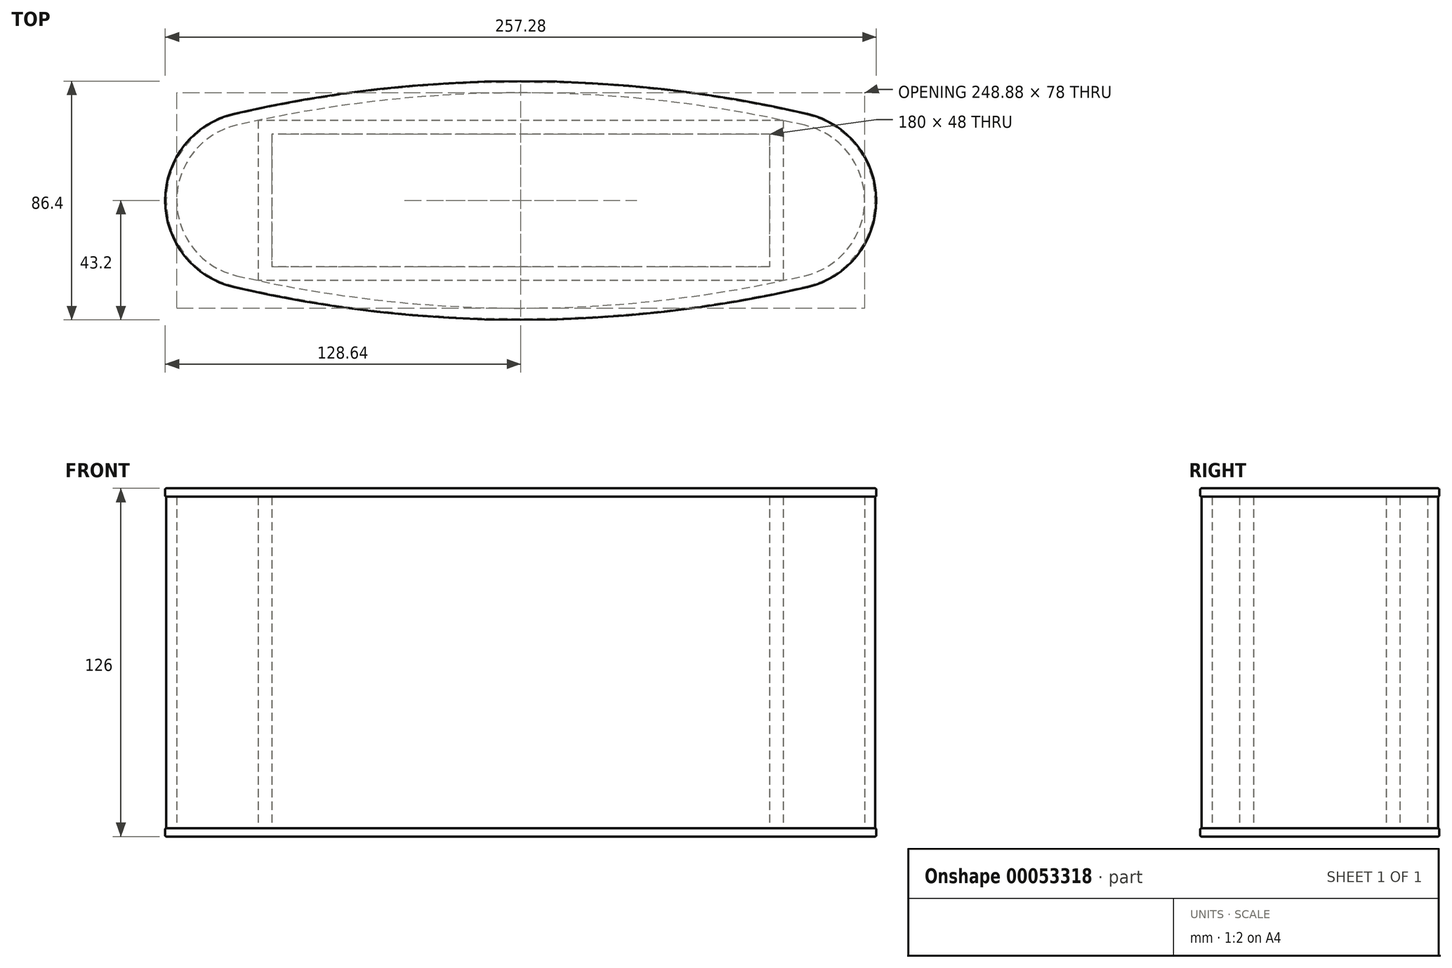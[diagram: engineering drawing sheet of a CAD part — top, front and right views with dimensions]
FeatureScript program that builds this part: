
annotation { "Feature Type Name" : "Feature", "Feature Type Description" : "" }
export const myFeature = defineFeature(function(context is Context, id is Id, definition is map)
    precondition{}
    {
        {
            var Q0;
            Q0=qCreatedBy(makeId("Top.planeOp"),FACE);
            var sketch = newSketch(context, id + "F0", { "sketchPlane" : qUnion([Q0])});
            skLineSegment(sketch, "E0.rect.bottom", {"start": v(90, 24) * mm, "end": v(-90, 24) * mm});
            skLineSegment(sketch, "E0.rect.top", {"start": v(90, -24) * mm, "end": v(-90, -24) * mm});
            skLineSegment(sketch, "E0.rect.left", {"start": v(90, 24) * mm, "end": v(90, -24) * mm});
            skLineSegment(sketch, "E0.rect.right", {"start": v(-90, 24) * mm, "end": v(-90, -24) * mm});
            skPoint(sketch, "E0.rect.middle", {"position": v(0, 0) * mm});
            skLineSegment(sketch, "E1.rect.bottom", {"start": v(95, 29) * mm, "end": v(-95, 29) * mm});
            skLineSegment(sketch, "E1.rect.top", {"start": v(95, -29) * mm, "end": v(-95, -29) * mm});
            skLineSegment(sketch, "E1.rect.left", {"start": v(95, 29) * mm, "end": v(95, -29) * mm});
            skLineSegment(sketch, "E1.rect.right", {"start": v(-95, 29) * mm, "end": v(-95, -29) * mm});
            skArc(sketch, "E2", {"start": v(102.74, 27.28) * mm, "mid": v(0, 39) * mm, "end": v(-102.74, 27.28) * mm});
            skArc(sketch, "E3", {"start": v(-102.74, -27.28) * mm, "mid": v(0, -39) * mm, "end": v(102.74, -27.28) * mm});
            skArc(sketch, "E4", {"start": v(-102.74, 27.28) * mm, "mid": v(-124.44, 0) * mm, "end": v(-102.74, -27.28) * mm});
            skArc(sketch, "E5", {"start": v(102.74, -27.28) * mm, "mid": v(124.44, 0) * mm, "end": v(102.74, 27.28) * mm});
            skArc(sketch, "E6.0", {"start": v(103.6, 30.98) * mm, "mid": v(0, 42.8) * mm, "end": v(-103.6, 30.98) * mm});
            skArc(sketch, "E6.1", {"start": v(103.6, -30.98) * mm, "mid": v(128.24, 0) * mm, "end": v(103.6, 30.98) * mm});
            skArc(sketch, "E6.2", {"start": v(-103.6, -30.98) * mm, "mid": v(0, -42.8) * mm, "end": v(103.6, -30.98) * mm});
            skArc(sketch, "E6.3", {"start": v(-103.6, 30.98) * mm, "mid": v(-128.24, 0) * mm, "end": v(-103.6, -30.98) * mm});
            skArc(sketch, "E7.0", {"start": v(103.7, 31.37) * mm, "mid": v(0, 43.2) * mm, "end": v(-103.7, 31.37) * mm});
            skArc(sketch, "E7.1", {"start": v(103.7, -31.37) * mm, "mid": v(128.64, 0) * mm, "end": v(103.7, 31.37) * mm});
            skArc(sketch, "E7.2", {"start": v(-103.7, -31.37) * mm, "mid": v(0, -43.2) * mm, "end": v(103.7, -31.37) * mm});
            skArc(sketch, "E7.3", {"start": v(-103.7, 31.37) * mm, "mid": v(-128.64, 0) * mm, "end": v(-103.7, -31.37) * mm});
            skSolve(sketch);
        }
        {
            var Q0;
            {var subQ5=sQuery(id+"F0.wireOp",EDGE,"E4");Q0=makeQuery(id+"F0.imprint","IMPRINT",FACE,{"disambiguationData":[TD([[makeQuery(id+"F0.imprint","IMPRINT",EDGE,{"derivedFrom":subQ5}),-1.0]])]});}
            var Q1;
            Q1=makeQuery(id+"F0.imprint","IMPRINT",FACE,{"disambiguationData":[TD([[makeQuery(id+"F0.imprint","IMPRINT",EDGE,{"derivedFrom":sQuery(id+"F0.wireOp",EDGE,"E0.rect.bottom")}),-1.0]])]});
            extrude(context, id + "F1", {"entities" : qUnion([Q0, Q1]), "depth" : 120 * mm});
        }
        {
            var Q0;
            Q0=qSketchRegion(id+"F0",true);
            var Q1;
            Q1=makeQuery(id+"F1.opExtrude","CAP_FACE",FACE,{"disambiguationData":[OSD([sQuery(id+"F0.wireOp",EDGE,"E2"),sQuery(id+"F0.wireOp",EDGE,"E3"),sQuery(id+"F0.wireOp",EDGE,"E4"),sQuery(id+"F0.wireOp",EDGE,"E5"),sQuery(id+"F0.wireOp",EDGE,"E6.0"),sQuery(id+"F0.wireOp",EDGE,"E6.1"),sQuery(id+"F0.wireOp",EDGE,"E6.2"),sQuery(id+"F0.wireOp",EDGE,"E6.3")])],"isStart":true});
            var Q2;
            {var subQ0=sQuery(id+"F0.wireOp",EDGE,"E1.rect.left");Q2=makeQuery(id+"F0.imprint","IMPRINT",FACE,{"disambiguationData":[TD([[makeQuery(id+"F0.imprint","IMPRINT",EDGE,{"derivedFrom":subQ0}),1.0]])]});}
            var Q3;
            {var subQ0=sQuery(id+"F0.wireOp",EDGE,"E1.rect.bottom");Q3=makeQuery(id+"F0.imprint","IMPRINT",FACE,{"disambiguationData":[TD([[makeQuery(id+"F0.imprint","IMPRINT",EDGE,{"derivedFrom":subQ0}),-1.0]])]});}
            var Q4;
            Q4=makeQuery(id+"F0.imprint","IMPRINT",FACE,{"disambiguationData":[TD([[makeQuery(id+"F0.imprint","IMPRINT",EDGE,{"derivedFrom":sQuery(id+"F0.wireOp",EDGE,"E0.rect.bottom")}),-1.0]])]});
            var Q5;
            Q5=makeQuery(id+"F0.imprint","IMPRINT",FACE,{"disambiguationData":[TD([[makeQuery(id+"F0.imprint","IMPRINT",EDGE,{"derivedFrom":sQuery(id+"F0.wireOp",EDGE,"E0.rect.bottom")}),1.0]])]});
            var Q6;
            {var subQ0=sQuery(id+"F0.wireOp",EDGE,"E1.rect.top");Q6=makeQuery(id+"F0.imprint","IMPRINT",FACE,{"disambiguationData":[TD([[makeQuery(id+"F0.imprint","IMPRINT",EDGE,{"derivedFrom":subQ0}),1.0]])]});}
            var Q7;
            {var subQ0=sQuery(id+"F0.wireOp",EDGE,"E1.rect.right");Q7=makeQuery(id+"F0.imprint","IMPRINT",FACE,{"disambiguationData":[TD([[makeQuery(id+"F0.imprint","IMPRINT",EDGE,{"derivedFrom":subQ0}),-1.0]])]});}
            extrude(context, id + "F2", {"entities" : qUnion([Q0, Q1, Q2, Q3, Q4, Q5, Q6, Q7]), "oppositeDirection" : true, "depth" : 3 * mm});
        }
        {
            var Q0;
            Q0=makeQuery(id+"F2.opExtrude","SWEPT_BODY",BODY,{"disambiguationData":[OSD([sQuery(id+"F0.wireOp",EDGE,"E2"),sQuery(id+"F0.wireOp",EDGE,"E3"),sQuery(id+"F0.wireOp",EDGE,"E4"),sQuery(id+"F0.wireOp",EDGE,"E5"),sQuery(id+"F0.wireOp",EDGE,"E6.0"),sQuery(id+"F0.wireOp",EDGE,"E6.1"),sQuery(id+"F0.wireOp",EDGE,"E6.2"),sQuery(id+"F0.wireOp",EDGE,"E6.3")])]});
            var Q1;
            Q1=makeQuery(id+"F2.opExtrude","SWEPT_BODY",BODY,{"disambiguationData":[OSD([sQuery(id+"F0.wireOp",EDGE,"E6.0"),sQuery(id+"F0.wireOp",EDGE,"E6.1"),sQuery(id+"F0.wireOp",EDGE,"E6.2"),sQuery(id+"F0.wireOp",EDGE,"E6.3"),sQuery(id+"F0.wireOp",EDGE,"E7.0"),sQuery(id+"F0.wireOp",EDGE,"E7.1"),sQuery(id+"F0.wireOp",EDGE,"E7.2"),sQuery(id+"F0.wireOp",EDGE,"E7.3")])]});
            booleanBodies(context, id + "F3", {"operationType" : BooleanOperationType.UNION, "tools" : qUnion([Q0, Q1])});
        }
        {
            var Q0;
            Q0=makeQuery(id+"F2.opExtrude","SWEPT_BODY",BODY,{"disambiguationData":[OSD([sQuery(id+"F0.wireOp",EDGE,"E2"),sQuery(id+"F0.wireOp",EDGE,"E3"),sQuery(id+"F0.wireOp",EDGE,"E4"),sQuery(id+"F0.wireOp",EDGE,"E5")])]});
            var Q1;
            Q1=makeQuery(id+"F2.opExtrude","SWEPT_BODY",BODY,{"disambiguationData":[OSD([sQuery(id+"F0.wireOp",EDGE,"E2"),sQuery(id+"F0.wireOp",EDGE,"E3"),sQuery(id+"F0.wireOp",EDGE,"E4"),sQuery(id+"F0.wireOp",EDGE,"E5"),sQuery(id+"F0.wireOp",EDGE,"E6.0"),sQuery(id+"F0.wireOp",EDGE,"E6.1"),sQuery(id+"F0.wireOp",EDGE,"E6.2"),sQuery(id+"F0.wireOp",EDGE,"E6.3")])]});
            booleanBodies(context, id + "F4", {"operationType" : BooleanOperationType.UNION, "tools" : qUnion([Q0, Q1])});
        }
        {
            var Q0;
            Q0=makeQuery(id+"F1.opExtrude","CAP_FACE",FACE,{"disambiguationData":[OSD([sQuery(id+"F0.wireOp",EDGE,"E2"),sQuery(id+"F0.wireOp",EDGE,"E3"),sQuery(id+"F0.wireOp",EDGE,"E4"),sQuery(id+"F0.wireOp",EDGE,"E5"),sQuery(id+"F0.wireOp",EDGE,"E6.0"),sQuery(id+"F0.wireOp",EDGE,"E6.1"),sQuery(id+"F0.wireOp",EDGE,"E6.2"),sQuery(id+"F0.wireOp",EDGE,"E6.3")])],"isStart":false});
            var sketch = newSketch(context, id + "F5", { "sketchPlane" : qUnion([Q0])});
            skArc(sketch, "E8.0", {"start": v(-103.7, -31.37) * mm, "mid": v(0, -43.2) * mm, "end": v(103.7, -31.37) * mm});
            skArc(sketch, "E9.0", {"start": v(103.7, -31.37) * mm, "mid": v(128.64, 0) * mm, "end": v(103.7, 31.37) * mm});
            skArc(sketch, "E10.0", {"start": v(-103.7, 31.37) * mm, "mid": v(-128.64, 0) * mm, "end": v(-103.7, -31.37) * mm});
            skArc(sketch, "E11.0", {"start": v(103.7, 31.37) * mm, "mid": v(0, 43.2) * mm, "end": v(-103.7, 31.37) * mm});
            skSolve(sketch);
        }
        {
            var Q0;
            Q0=qSketchRegion(id+"F5",true);
            extrude(context, id + "F6", {"entities" : qUnion([Q0]), "depth" : 3 * mm});
        }
        {
            var Q0;
            Q0=makeQuery(id+"F6.opExtrude","CAP_FACE",FACE,{"disambiguationData":[OSD([sQuery(id+"F5.wireOp",EDGE,"E8.0"),sQuery(id+"F5.wireOp",EDGE,"E9.0"),sQuery(id+"F5.wireOp",EDGE,"E10.0"),sQuery(id+"F5.wireOp",EDGE,"E11.0")])],"isStart":false});
            var Q1;
            {var subQ0=sQuery(id+"F0.wireOp",EDGE,"E6.3");var subQ1=sQuery(id+"F0.wireOp",EDGE,"E6.2");var subQ2=sQuery(id+"F0.wireOp",EDGE,"E6.1");var subQ3=sQuery(id+"F0.wireOp",EDGE,"E6.0");var subQ4=sQuery(id+"F0.wireOp",EDGE,"E5");var subQ5=sQuery(id+"F0.wireOp",EDGE,"E4");var subQ6=sQuery(id+"F0.wireOp",EDGE,"E3");var subQ7=sQuery(id+"F0.wireOp",EDGE,"E2");Q1=makeQuery(id+"F4.opBoolean","MERGE",FACE,{"derivedFrom":[makeQuery(id+"F2.opExtrude","CAP_FACE",FACE,{"disambiguationData":[OSD([subQ7,subQ6,subQ5,subQ4])],"isStart":true}),makeQuery(id+"F3.opBoolean","MERGE",FACE,{"derivedFrom":[makeQuery(id+"F2.opExtrude","CAP_FACE",FACE,{"disambiguationData":[OSD([subQ3,subQ2,subQ1,subQ0,sQuery(id+"F0.wireOp",EDGE,"E7.0"),sQuery(id+"F0.wireOp",EDGE,"E7.1"),sQuery(id+"F0.wireOp",EDGE,"E7.2"),sQuery(id+"F0.wireOp",EDGE,"E7.3")])],"isStart":true}),makeQuery(id+"F2.opExtrude","CAP_FACE",FACE,{"disambiguationData":[OSD([subQ7,subQ6,subQ5,subQ4,subQ3,subQ2,subQ1,subQ0])],"isStart":true})]})]});}
            var Q2;
            Q2=makeQuery(id+"F6.opExtrude","CAP_FACE",FACE,{"disambiguationData":[OSD([sQuery(id+"F5.wireOp",EDGE,"E8.0"),sQuery(id+"F5.wireOp",EDGE,"E9.0"),sQuery(id+"F5.wireOp",EDGE,"E10.0"),sQuery(id+"F5.wireOp",EDGE,"E11.0")])],"isStart":true});
            var Q3;
            {var subQ0=sQuery(id+"F0.wireOp",EDGE,"E6.3");var subQ1=sQuery(id+"F0.wireOp",EDGE,"E6.2");var subQ2=sQuery(id+"F0.wireOp",EDGE,"E6.1");var subQ3=sQuery(id+"F0.wireOp",EDGE,"E6.0");var subQ4=sQuery(id+"F0.wireOp",EDGE,"E5");var subQ5=sQuery(id+"F0.wireOp",EDGE,"E4");var subQ6=sQuery(id+"F0.wireOp",EDGE,"E3");var subQ7=sQuery(id+"F0.wireOp",EDGE,"E2");Q3=makeQuery(id+"F4.opBoolean","MERGE",FACE,{"derivedFrom":[makeQuery(id+"F2.opExtrude","CAP_FACE",FACE,{"disambiguationData":[OSD([subQ7,subQ6,subQ5,subQ4])],"isStart":false}),makeQuery(id+"F3.opBoolean","MERGE",FACE,{"derivedFrom":[makeQuery(id+"F2.opExtrude","CAP_FACE",FACE,{"disambiguationData":[OSD([subQ3,subQ2,subQ1,subQ0,sQuery(id+"F0.wireOp",EDGE,"E7.0"),sQuery(id+"F0.wireOp",EDGE,"E7.1"),sQuery(id+"F0.wireOp",EDGE,"E7.2"),sQuery(id+"F0.wireOp",EDGE,"E7.3")])],"isStart":false}),makeQuery(id+"F2.opExtrude","CAP_FACE",FACE,{"disambiguationData":[OSD([subQ7,subQ6,subQ5,subQ4,subQ3,subQ2,subQ1,subQ0])],"isStart":false})]})]});}
            fillet(context, id + "F7", {"entities" : qUnion([Q0, Q1, Q2, Q3]), "radius" : 0.4 * mm, "tangentPropagation" : true, "allowEdgeOverflow" : false});
        }
    });
